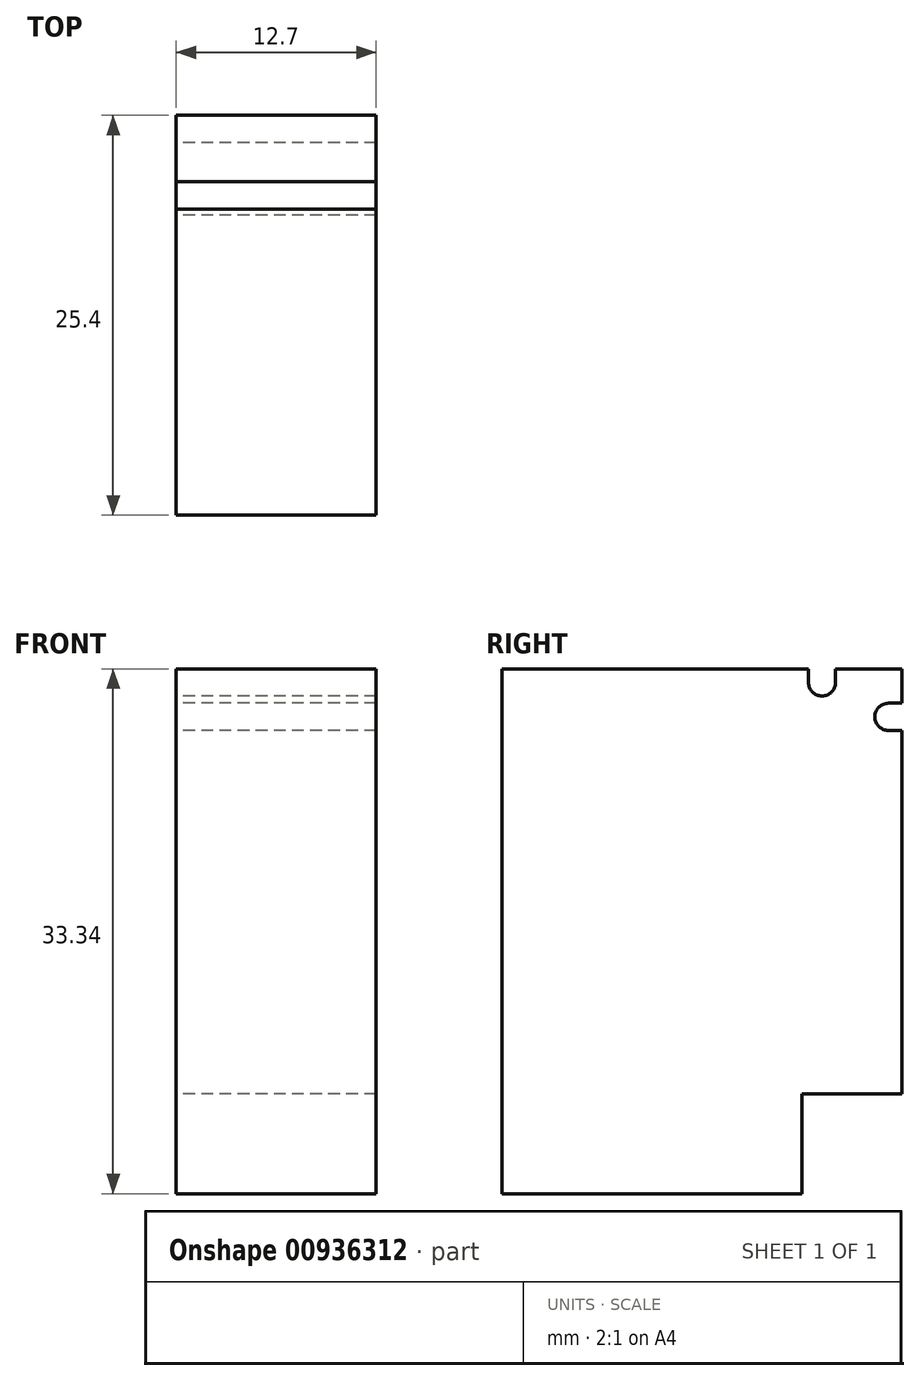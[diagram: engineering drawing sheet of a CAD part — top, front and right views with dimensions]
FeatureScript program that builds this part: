
annotation { "Feature Type Name" : "Feature", "Feature Type Description" : "" }
export const myFeature = defineFeature(function(context is Context, id is Id, definition is map)
    precondition{}
    {
        {
            var Q0;
            Q0=qCreatedBy(makeId("Right.planeOp"),FACE);
            var sketch = newSketch(context, id + "F0", { "sketchPlane" : qUnion([Q0])});
            skLineSegment(sketch, "E0.bottom", {"start": v(-34.47, 36.84) * mm, "end": v(-15.01, 36.84) * mm});
            skLineSegment(sketch, "E0.top", {"start": v(-34.47, 3.5) * mm, "end": v(-15.42, 3.5) * mm});
            skLineSegment(sketch, "E0.left", {"start": v(-34.47, 36.84) * mm, "end": v(-34.47, 3.5) * mm});
            skLineSegment(sketch, "E0.right", {"start": v(-9.07, 36.84) * mm, "end": v(-9.07, 34.65) * mm});
            skArc(sketch, "E1", {"start": v(-15.01, 35.97) * mm, "mid": v(-14.15, 35.11) * mm, "end": v(-13.28, 35.97) * mm});
            skArc(sketch, "E2", {"start": v(-9.93, 34.65) * mm, "mid": v(-10.8, 33.8) * mm, "end": v(-9.93, 32.93) * mm});
            skLineSegment(sketch, "E3", {"start": v(-15.01, 35.97) * mm, "end": v(-15.01, 36.84) * mm});
            skLineSegment(sketch, "E4", {"start": v(-13.28, 35.97) * mm, "end": v(-13.28, 36.84) * mm});
            skLineSegment(sketch, "E5.trimOffspring", {"start": v(-13.28, 36.84) * mm, "end": v(-9.07, 36.84) * mm});
            skLineSegment(sketch, "E6", {"start": v(-9.93, 32.93) * mm, "end": v(-9.07, 32.93) * mm});
            skLineSegment(sketch, "E7", {"start": v(-9.93, 34.65) * mm, "end": v(-9.07, 34.65) * mm});
            skLineSegment(sketch, "E8.trimOffspring", {"start": v(-9.07, 32.93) * mm, "end": v(-9.07, 9.85) * mm});
            skLineSegment(sketch, "E9.top", {"start": v(-9.07, 9.85) * mm, "end": v(-15.42, 9.85) * mm});
            skLineSegment(sketch, "E9.right", {"start": v(-15.42, 3.5) * mm, "end": v(-15.42, 9.85) * mm});
            skSolve(sketch);
        }
        {
            var Q0;
            Q0=makeQuery(id+"F0.imprint","IMPRINT",FACE,{"disambiguationData":[TD([[makeQuery(id+"F0.imprint","IMPRINT",EDGE,{"derivedFrom":sQuery(id+"F0.wireOp",EDGE,"E0.bottom")}),-1.0]])]});
            extrude(context, id + "F1", {"entities" : qUnion([Q0]), "depth" : 12.7 * mm, "offsetDistance" : 25.4 * mm});
        }
    });
